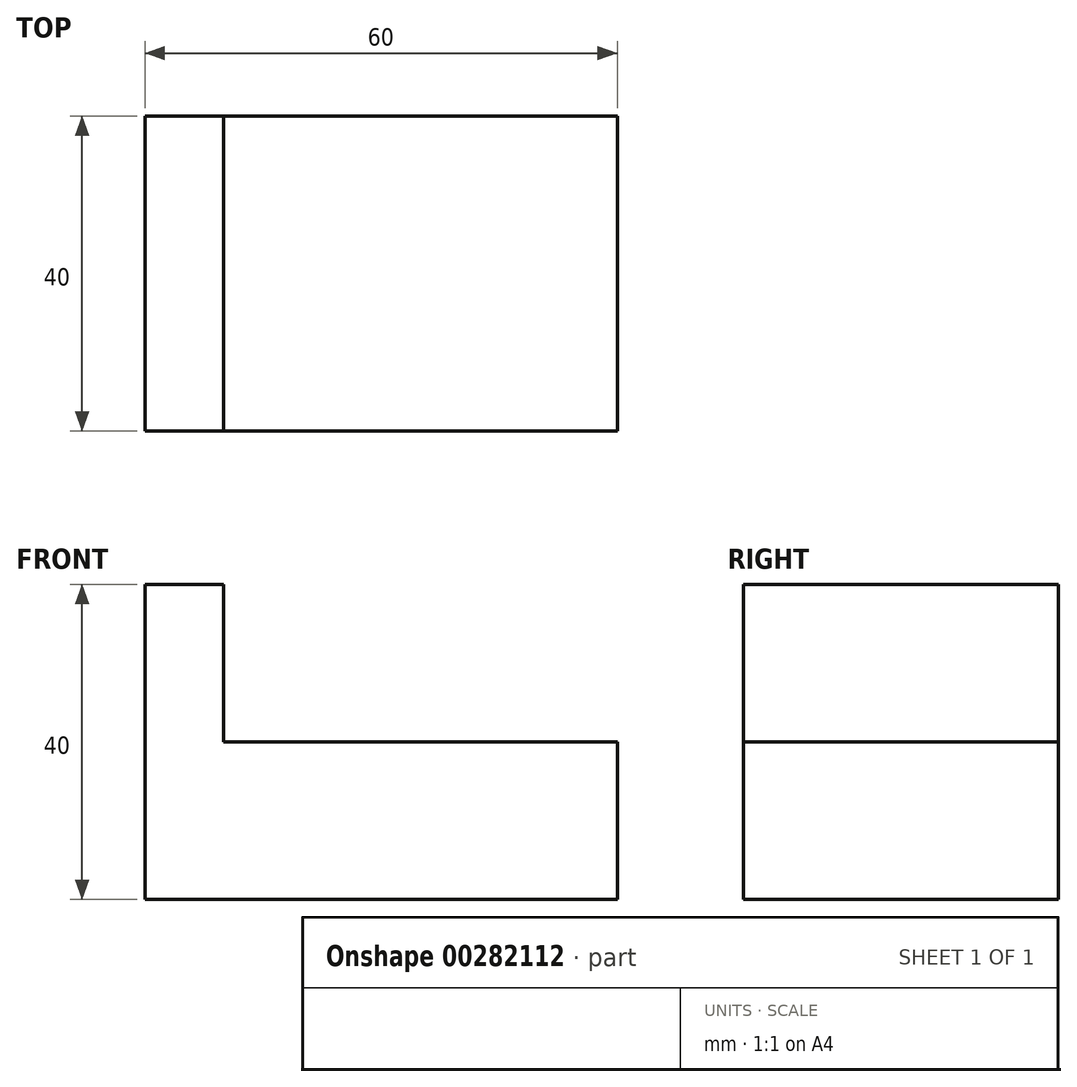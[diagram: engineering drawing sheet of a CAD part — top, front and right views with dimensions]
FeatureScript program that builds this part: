
annotation { "Feature Type Name" : "Feature", "Feature Type Description" : "" }
export const myFeature = defineFeature(function(context is Context, id is Id, definition is map)
    precondition{}
    {
        {
            var Q0;
            Q0=qCreatedBy(makeId("Front.planeOp"),FACE);
            var sketch = newSketch(context, id + "F0", { "sketchPlane" : qUnion([Q0])});
            skLineSegment(sketch, "E0", {"start": v(38.75, 0) * mm, "end": v(-21.25, 0) * mm});
            skLineSegment(sketch, "E1", {"start": v(-21.25, 0) * mm, "end": v(-21.25, 40) * mm});
            skLineSegment(sketch, "E2", {"start": v(-21.25, 40) * mm, "end": v(-11.25, 40) * mm});
            skLineSegment(sketch, "E3", {"start": v(-11.25, 40) * mm, "end": v(-11.25, 20) * mm});
            skLineSegment(sketch, "E4", {"start": v(-11.25, 20) * mm, "end": v(38.75, 20) * mm});
            skLineSegment(sketch, "E5", {"start": v(38.75, 20) * mm, "end": v(38.75, 0) * mm});
            skSolve(sketch);
        }
        {
            var Q0;
            Q0=makeQuery(id+"F0.imprint","IMPRINT",FACE,{"disambiguationData":[TD([[makeQuery(id+"F0.imprint","IMPRINT",EDGE,{"derivedFrom":sQuery(id+"F0.wireOp",EDGE,"E0")}),-1.0]])]});
            extrude(context, id + "F1", {"entities" : qUnion([Q0]), "oppositeDirection" : true, "depth" : 40 * mm});
        }
    });
